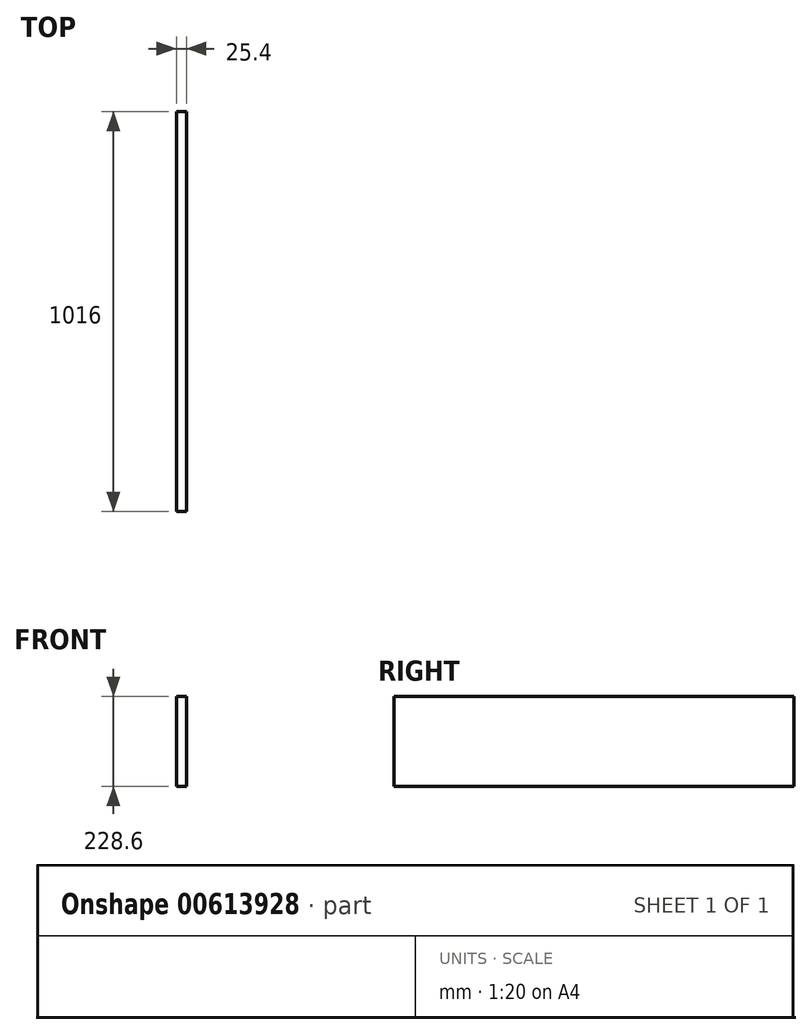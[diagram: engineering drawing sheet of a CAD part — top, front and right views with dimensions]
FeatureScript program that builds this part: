
annotation { "Feature Type Name" : "Feature", "Feature Type Description" : "" }
export const myFeature = defineFeature(function(context is Context, id is Id, definition is map)
    precondition{}
    {
        {
            var Q0;
            Q0=qCreatedBy(makeId("Right.planeOp"),FACE);
            var sketch = newSketch(context, id + "F0", { "sketchPlane" : qUnion([Q0])});
            skLineSegment(sketch, "E0.bottom", {"start": v(732.3, 113.44) * mm, "end": v(-283.7, 113.44) * mm});
            skLineSegment(sketch, "E0.top", {"start": v(732.3, -115.16) * mm, "end": v(-283.7, -115.16) * mm});
            skLineSegment(sketch, "E0.left", {"start": v(732.3, 113.44) * mm, "end": v(732.3, -115.16) * mm});
            skLineSegment(sketch, "E0.right", {"start": v(-283.7, 113.44) * mm, "end": v(-283.7, -115.16) * mm});
            skSolve(sketch);
        }
        {
            var Q0;
            Q0 = qSketchRegion(id + "F0", true);
            extrude(context, id + "F1", {"entities" : qUnion([Q0]), "depth" : 25.4 * mm, "offsetDistance" : 25.4 * mm});
        }
    });
